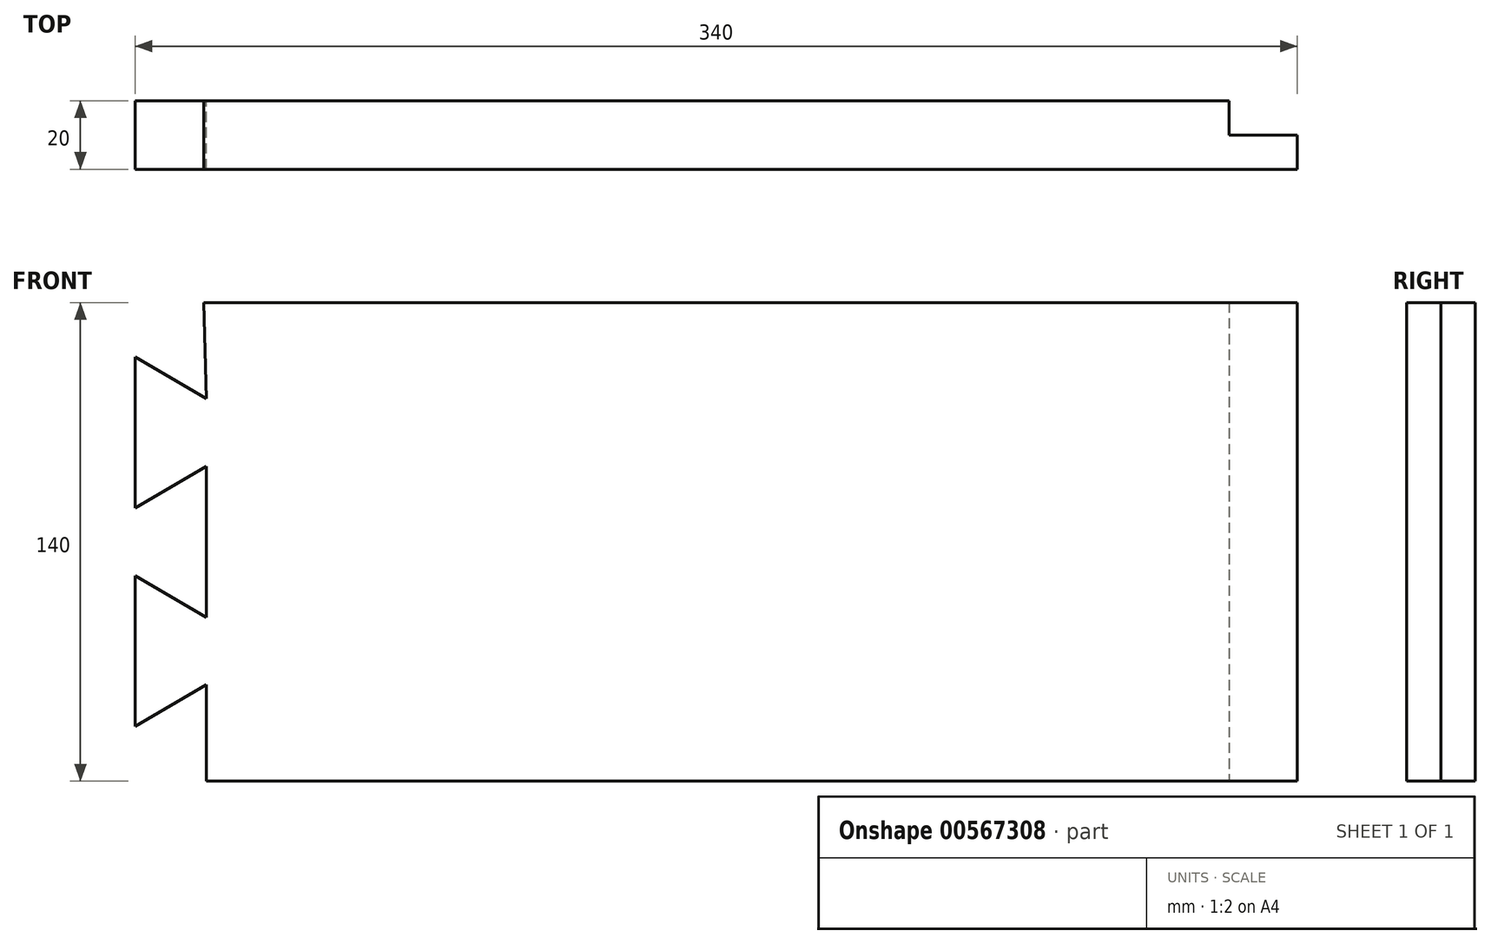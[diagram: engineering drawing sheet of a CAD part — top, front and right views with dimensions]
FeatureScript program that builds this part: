
annotation { "Feature Type Name" : "Feature", "Feature Type Description" : "" }
export const myFeature = defineFeature(function(context is Context, id is Id, definition is map)
    precondition{}
    {
        {
            var Q0;
            Q0=qCreatedBy(makeId("Front.planeOp"),FACE);
            var sketch = newSketch(context, id + "F0", { "sketchPlane" : qUnion([Q0])});
            skLineSegment(sketch, "E0.bottom", {"start": v(170, 70) * mm, "end": v(-170, 70) * mm});
            skLineSegment(sketch, "E0.top", {"start": v(170, -70) * mm, "end": v(-170, -70) * mm});
            skLineSegment(sketch, "E0.left", {"start": v(170, 70) * mm, "end": v(170, -70) * mm});
            skLineSegment(sketch, "E0.right", {"start": v(-170, 70) * mm, "end": v(-170, -70) * mm});
            skPoint(sketch, "E0.middle", {"position": v(0, 0) * mm});
            skSolve(sketch);
        }
        {
            var Q0;
            Q0=makeQuery(id+"F0.imprint","IMPRINT",FACE,{"disambiguationData":[TD([[makeQuery(id+"F0.imprint","IMPRINT",EDGE,{"derivedFrom":sQuery(id+"F0.wireOp",EDGE,"E0.bottom")}),1.0]])]});
            extrude(context, id + "F1", {"entities" : qUnion([Q0]), "depth" : 20 * mm, "offsetDistance" : 25.4 * mm});
        }
        {
            var Q0;
            Q0=makeQuery(id+"F1.opExtrude","SWEPT_FACE",FACE,{"disambiguationData":[OSD([sQuery(id+"F0.wireOp",EDGE,"E0.left")])]});
            var sketch = newSketch(context, id + "F2", { "sketchPlane" : qUnion([Q0])});
            skLineSegment(sketch, "E1.bottom", {"start": v(-20, 70) * mm, "end": v(-10, 70) * mm});
            skLineSegment(sketch, "E1.top", {"start": v(-20, -70) * mm, "end": v(-10, -70) * mm});
            skLineSegment(sketch, "E1.left", {"start": v(-20, 70) * mm, "end": v(-20, -70) * mm});
            skLineSegment(sketch, "E1.right", {"start": v(-10, 70) * mm, "end": v(-10, -70) * mm});
            skSolve(sketch);
        }
        {
            var Q0;
            Q0=makeQuery(id+"F1.opExtrude","CAP_FACE",FACE,{"disambiguationData":[OSD([sQuery(id+"F0.wireOp",EDGE,"E0.bottom"),sQuery(id+"F0.wireOp",EDGE,"E0.top"),sQuery(id+"F0.wireOp",EDGE,"E0.left"),sQuery(id+"F0.wireOp",EDGE,"E0.right")])],"isStart":true});
            var sketch = newSketch(context, id + "F3", { "sketchPlane" : qUnion([Q0])});
            skLineSegment(sketch, "E2.bottom", {"start": v(170, 70) * mm, "end": v(150, 70) * mm});
            skLineSegment(sketch, "E2.top", {"start": v(170, -70) * mm, "end": v(150, -70) * mm});
            skLineSegment(sketch, "E2.left", {"start": v(170, 70) * mm, "end": v(170, -70) * mm});
            skLineSegment(sketch, "E3", {"start": v(170, 0) * mm, "end": v(150, 0) * mm});
            skLineSegment(sketch, "E4", {"start": v(170, 0) * mm, "end": v(170, 9.88) * mm});
            skLineSegment(sketch, "E5", {"start": v(170, 9.88) * mm, "end": v(149.18, 22.07) * mm});
            skLineSegment(sketch, "E6", {"start": v(149.18, 22.07) * mm, "end": v(149.18, 41.84) * mm});
            skLineSegment(sketch, "E7", {"start": v(149.18, 41.84) * mm, "end": v(170, 54.03) * mm});
            skLineSegment(sketch, "E8", {"start": v(170, 54.03) * mm, "end": v(170, 70) * mm});
            skLineSegment(sketch, "E9.MirrorCS", {"start": v(170, 0) * mm, "end": v(170, -9.88) * mm});
            skLineSegment(sketch, "E10.MirrorCS", {"start": v(170, -9.88) * mm, "end": v(149.18, -22.07) * mm});
            skLineSegment(sketch, "E11.MirrorCS", {"start": v(149.18, -22.07) * mm, "end": v(149.18, -41.84) * mm});
            skLineSegment(sketch, "E12.MirrorCS", {"start": v(149.18, -41.84) * mm, "end": v(170, -54.03) * mm});
            skLineSegment(sketch, "E13", {"start": v(149.18, 22.07) * mm, "end": v(149.18, -22.07) * mm});
            skLineSegment(sketch, "E14", {"start": v(149.18, 41.84) * mm, "end": v(150, 70) * mm});
            skLineSegment(sketch, "E15", {"start": v(149.18, -41.84) * mm, "end": v(149.18, -70) * mm});
            skLineSegment(sketch, "E16", {"start": v(149.18, -70) * mm, "end": v(170, -70) * mm});
            skLineSegment(sketch, "E17", {"start": v(150, 70) * mm, "end": v(170, 70) * mm});
            skSolve(sketch);
        }
        {
            var Q0;
            {var subQ0=sQuery(id+"F3.wireOp",EDGE,"E12.MirrorCS");Q0=makeQuery(id+"F3.imprint","IMPRINT",FACE,{"disambiguationData":[TD([[makeQuery(id+"F3.imprint","IMPRINT",EDGE,{"derivedFrom":subQ0}),-1.0]])]});}
            var Q1;
            {var subQ0=sQuery(id+"F3.wireOp",EDGE,"E7");Q1=makeQuery(id+"F3.imprint","IMPRINT",FACE,{"disambiguationData":[TD([[makeQuery(id+"F3.imprint","IMPRINT",EDGE,{"derivedFrom":subQ0}),1.0]])]});}
            var Q2;
            {var subQ2=sQuery(id+"F3.wireOp",EDGE,"E5");Q2=makeQuery(id+"F3.imprint","IMPRINT",FACE,{"disambiguationData":[TD([[makeQuery(id+"F3.imprint","IMPRINT",EDGE,{"derivedFrom":subQ2}),1.0]])]});}
            extrude(context, id + "F4", {"entities" : qUnion([Q0, Q1, Q2]), "operationType" : NewBodyOperationType.REMOVE, "oppositeDirection" : true, "depth" : 20 * mm, "offsetDistance" : 25 * mm});
        }
        {
            var Q0;
            {var subQ0=sQuery(id+"F2.wireOp",EDGE,"E1.right");Q0=makeQuery(id+"F2.imprint","IMPRINT",FACE,{"disambiguationData":[TD([[makeQuery(id+"F2.imprint","IMPRINT",EDGE,{"derivedFrom":subQ0}),1.0]])]});}
            extrude(context, id + "F5", {"entities" : qUnion([Q0]), "operationType" : NewBodyOperationType.REMOVE, "oppositeDirection" : true, "depth" : 20 * mm, "offsetDistance" : 25 * mm});
        }
        {
            var Q0;
            Q0=makeQuery(id+"F1.opExtrude","CAP_FACE",FACE,{"disambiguationData":[OSD([sQuery(id+"F0.wireOp",EDGE,"E0.bottom"),sQuery(id+"F0.wireOp",EDGE,"E0.top"),sQuery(id+"F0.wireOp",EDGE,"E0.left"),sQuery(id+"F0.wireOp",EDGE,"E0.right")])],"isStart":true});
            var sketch = newSketch(context, id + "F6", { "sketchPlane" : qUnion([Q0])});
            skLineSegment(sketch, "E18.bottom", {"start": v(149.18, -70) * mm, "end": v(-150, -70) * mm});
            skLineSegment(sketch, "E18.top", {"start": v(149.18, -60) * mm, "end": v(-150, -60) * mm});
            skLineSegment(sketch, "E18.left", {"start": v(149.18, -70) * mm, "end": v(149.18, -60) * mm});
            skLineSegment(sketch, "E18.right", {"start": v(-150, -70) * mm, "end": v(-150, -60) * mm});
            skLineSegment(sketch, "E19", {"start": v(150, 70) * mm, "end": v(-150, 70) * mm});
            skPoint(sketch, "E20", {"position": v(-0.41, -60) * mm});
            skLineSegment(sketch, "E21.bottom", {"start": v(-150, 70) * mm, "end": v(149.7, 70) * mm});
            skLineSegment(sketch, "E21.top", {"start": v(-150, 60) * mm, "end": v(149.7, 60) * mm});
            skLineSegment(sketch, "E21.left", {"start": v(-150, 70) * mm, "end": v(-150, 60) * mm});
            skLineSegment(sketch, "E21.right", {"start": v(149.7, 70) * mm, "end": v(149.7, 60) * mm});
            skPoint(sketch, "E22", {"position": v(-0.15, 60) * mm});
            skSolve(sketch);
        }
    });
